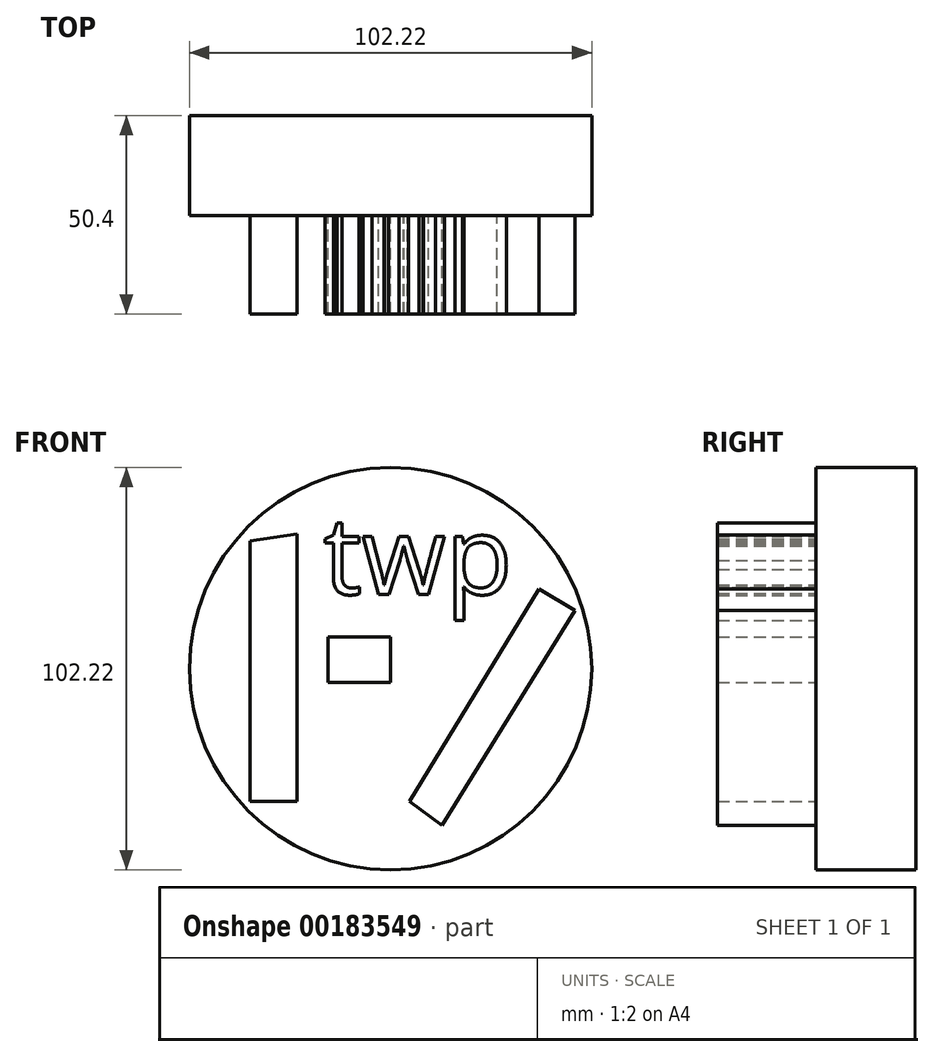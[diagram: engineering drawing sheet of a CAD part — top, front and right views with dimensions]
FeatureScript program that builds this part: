
annotation { "Feature Type Name" : "Feature", "Feature Type Description" : "" }
export const myFeature = defineFeature(function(context is Context, id is Id, definition is map)
    precondition{}
    {
        {
            var Q0;
            Q0=qCreatedBy(makeId("Front.planeOp"),FACE);
            var sketch = newSketch(context, id + "F0", { "sketchPlane" : qUnion([Q0])});
            skCircle(sketch, "E0", {"center": v(0, 0) * mm, "radius": 51.1 * mm});
            skSolve(sketch);
        }
        {
            var Q0;
            Q0 = qSketchRegion(id + "F0", true);
            extrude(context, id + "F1", {"entities" : qUnion([Q0]), "depth" : 25.4 * mm});
        }
        {
            var Q0;
            Q0=makeQuery(id+"F1.opExtrude","CAP_FACE",FACE,{"disambiguationData":[OSD([sQuery(id+"F0.wireOp",EDGE,"E0")])],"isStart":false});
            var sketch = newSketch(context, id + "F2", { "sketchPlane" : qUnion([Q0])});
            skLineSegment(sketch, "E1", {"start": v(-35.64, 32.45) * mm, "end": v(-35.64, -33.7) * mm});
            skLineSegment(sketch, "E2", {"start": v(-35.64, -33.7) * mm, "end": v(-23.76, -33.7) * mm});
            skLineSegment(sketch, "E3", {"start": v(-23.76, -33.7) * mm, "end": v(-23.76, 34.28) * mm});
            skLineSegment(sketch, "E4", {"start": v(-35.64, 32.45) * mm, "end": v(-23.76, 34.28) * mm});
            skLineSegment(sketch, "E5", {"start": v(-15.84, 8.06) * mm, "end": v(0, 8.06) * mm});
            skLineSegment(sketch, "E6", {"start": v(0, 8.06) * mm, "end": v(0, -3.52) * mm});
            skLineSegment(sketch, "E7", {"start": v(0, -3.52) * mm, "end": v(-15.84, -3.52) * mm});
            skLineSegment(sketch, "E8", {"start": v(-15.84, -3.52) * mm, "end": v(-15.84, 8.06) * mm});
            skLineSegment(sketch, "E9", {"start": v(4.87, -33.7) * mm, "end": v(13.1, -39.8) * mm});
            skLineSegment(sketch, "E10", {"start": v(13.1, -39.8) * mm, "end": v(4.87, -33.7) * mm});
            skLineSegment(sketch, "E11", {"start": v(4.87, -33.7) * mm, "end": v(37.78, 20.26) * mm});
            skLineSegment(sketch, "E12", {"start": v(37.78, 20.26) * mm, "end": v(46.8, 14.75) * mm});
            skLineSegment(sketch, "E13", {"start": v(46.8, 14.75) * mm, "end": v(13.1, -39.8) * mm});
            skSolve(sketch);
        }
        {
            var Q0;
            Q0 = qSketchRegion(id + "F2", true);
            extrude(context, id + "F3", {"entities" : qUnion([Q0]), "operationType" : NewBodyOperationType.ADD, "depth" : 25 * mm});
        }
        {
            var Q0;
            Q0=makeQuery(id+"F1.opExtrude","CAP_FACE",FACE,{"disambiguationData":[OSD([sQuery(id+"F0.wireOp",EDGE,"E0")])],"isStart":false});
            var sketch = newSketch(context, id + "F4", { "sketchPlane" : qUnion([Q0])});
            skText(sketch, "E14", { "text": "twp", "fontName": "OpenSans-Regular.ttf"});
            const initialGuessF4  = {"E14": [-0.01705, 0.01892, 1, 0, 0.01981]};
            skSetInitialGuess(sketch, initialGuessF4);
            skSolve(sketch);
        }
        {
            var Q0;
            Q0 = qSketchRegion(id + "F4", true);
            extrude(context, id + "F5", {"entities" : qUnion([Q0]), "operationType" : NewBodyOperationType.ADD, "depth" : 25 * mm});
        }
    });
